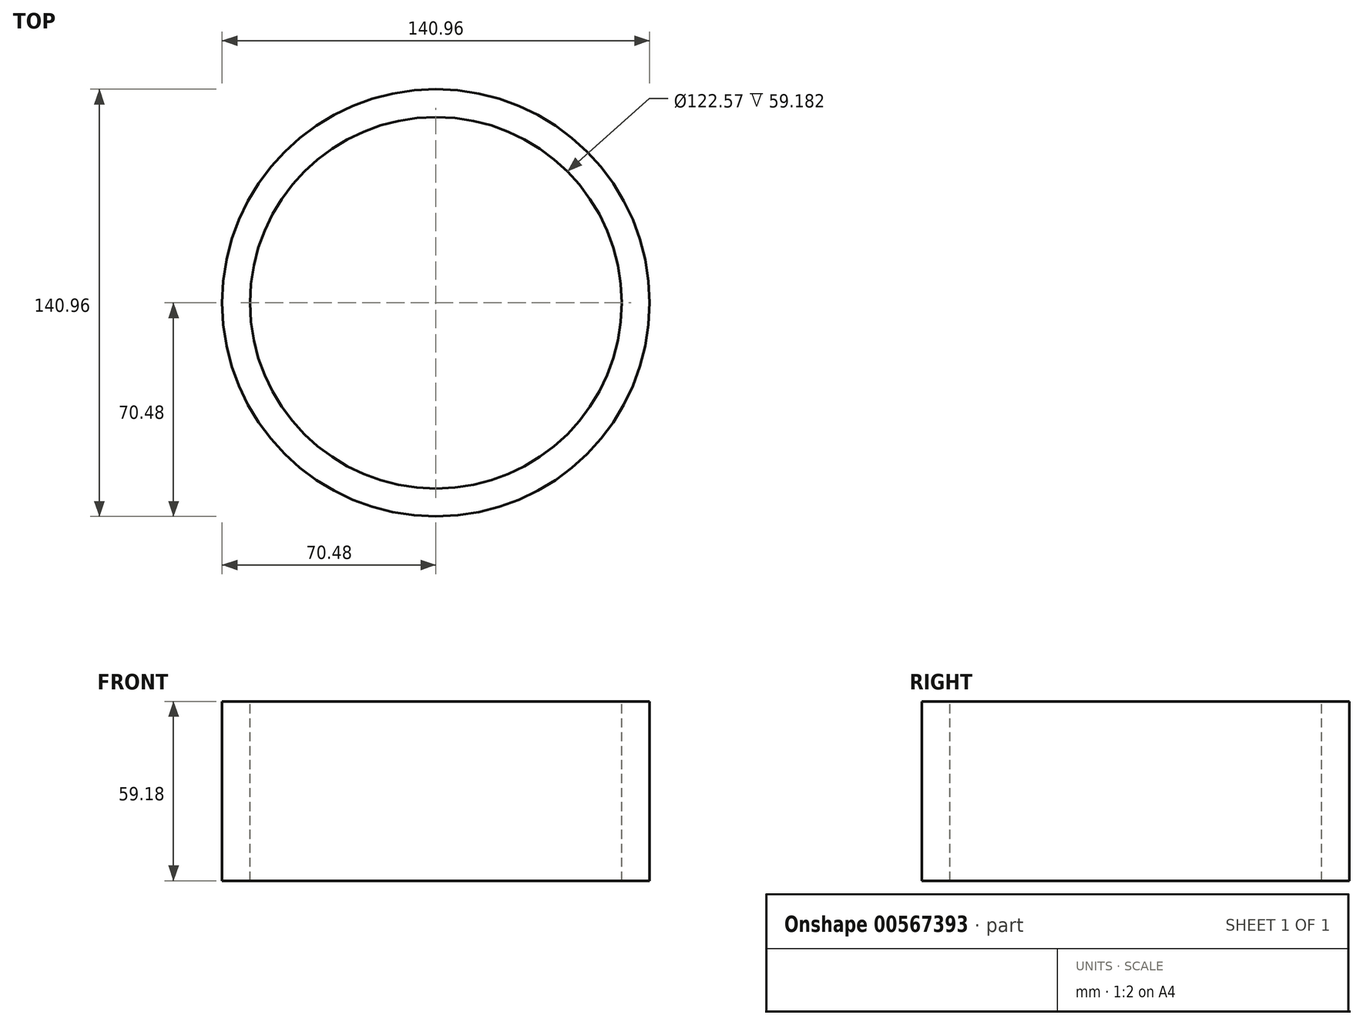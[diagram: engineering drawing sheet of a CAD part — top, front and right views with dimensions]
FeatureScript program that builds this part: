
annotation { "Feature Type Name" : "Feature", "Feature Type Description" : "" }
export const myFeature = defineFeature(function(context is Context, id is Id, definition is map)
    precondition{}
    {
        {
            var Q0;
            Q0=qCreatedBy(makeId("Top.planeOp"),FACE);
            var sketch = newSketch(context, id + "F0", { "sketchPlane" : qUnion([Q0])});
            skCircle(sketch, "E0", {"center": v(0, 0) * mm, "radius": 70.48 * mm});
            skCircle(sketch, "E1", {"center": v(0, 0) * mm, "radius": 61.28 * mm});
            skSolve(sketch);
        }
        {
            var Q0;
            Q0 = qSketchRegion(id + "F0", true);
            extrude(context, id + "F1", {"entities" : qUnion([Q0]), "oppositeDirection" : true, "depth" : 59.18 * mm, "offsetDistance" : 25.4 * mm});
        }
    });
